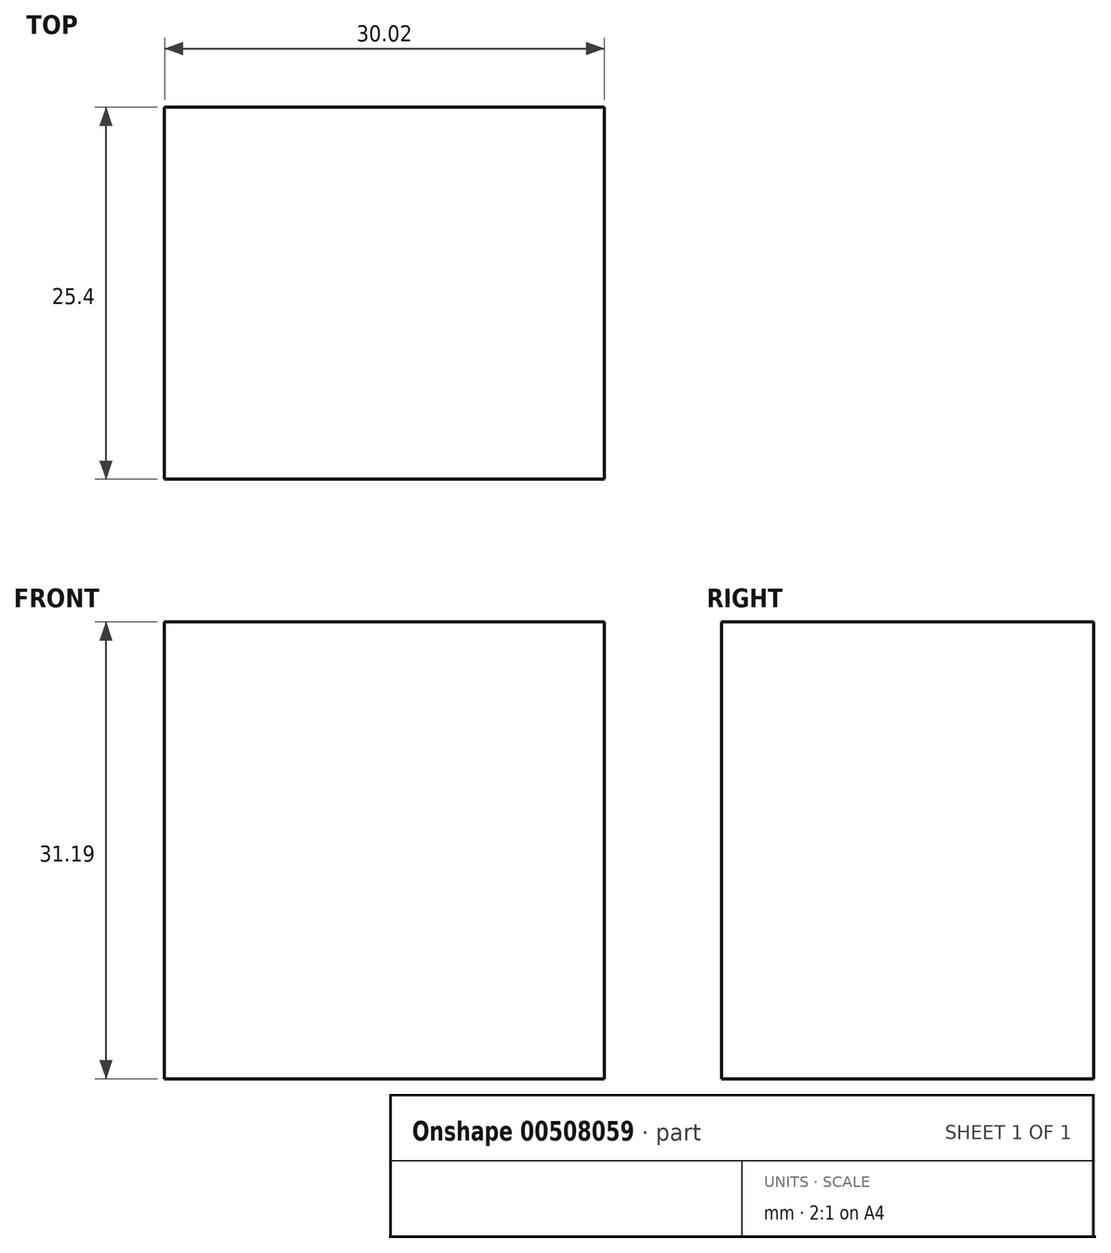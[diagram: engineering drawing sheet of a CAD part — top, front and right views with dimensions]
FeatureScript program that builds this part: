
annotation { "Feature Type Name" : "Feature", "Feature Type Description" : "" }
export const myFeature = defineFeature(function(context is Context, id is Id, definition is map)
    precondition{}
    {
        {
            var Q0;
            Q0=qCreatedBy(makeId("Front.planeOp"),FACE);
            var sketch = newSketch(context, id + "F0", { "sketchPlane" : qUnion([Q0])});
            skLineSegment(sketch, "E0.bottom", {"start": v(14, 12.39) * mm, "end": v(-16.03, 12.39) * mm});
            skLineSegment(sketch, "E0.top", {"start": v(14, -18.8) * mm, "end": v(-16.03, -18.8) * mm});
            skLineSegment(sketch, "E0.left", {"start": v(14, 12.39) * mm, "end": v(14, -18.8) * mm});
            skLineSegment(sketch, "E0.right", {"start": v(-16.03, 12.39) * mm, "end": v(-16.03, -18.8) * mm});
            skSolve(sketch);
        }
        {
            var Q0;
            Q0 = qSketchRegion(id + "F0", true);
            extrude(context, id + "F1", {"entities" : qUnion([Q0]), "endBound" : BoundingType.SYMMETRIC, "depth" : 25.4 * mm});
        }
    });
